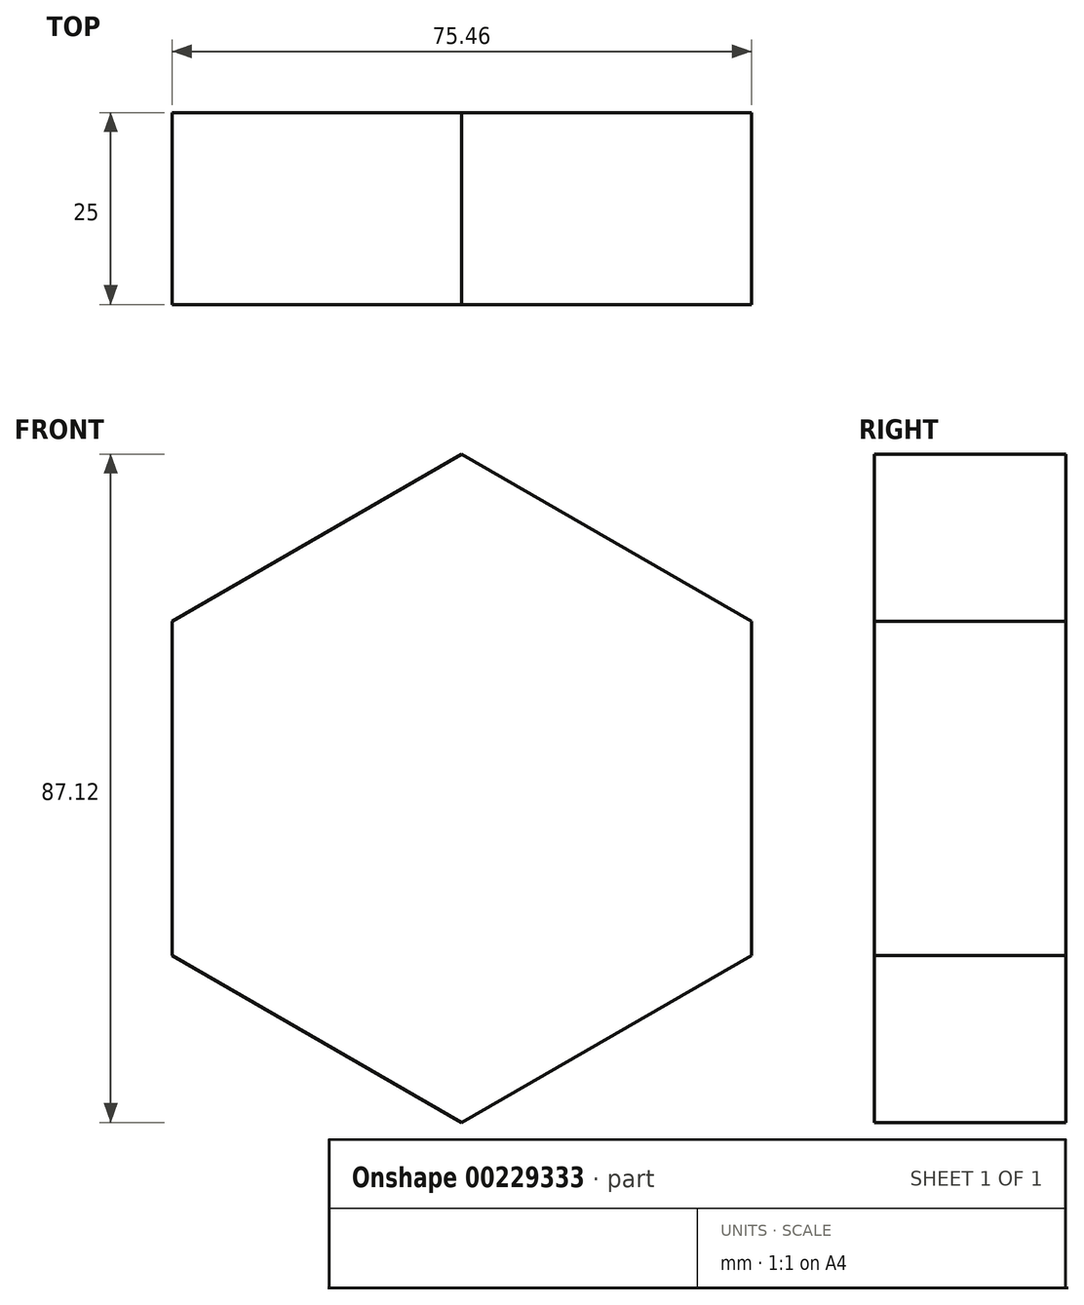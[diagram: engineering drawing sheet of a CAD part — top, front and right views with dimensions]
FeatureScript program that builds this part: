
annotation { "Feature Type Name" : "Feature", "Feature Type Description" : "" }
export const myFeature = defineFeature(function(context is Context, id is Id, definition is map)
    precondition{}
    {
        {
            var Q0;
            Q0=qCreatedBy(makeId("Front.planeOp"),FACE);
            var sketch = newSketch(context, id + "F0", { "sketchPlane" : qUnion([Q0])});
            skCircle(sketch, "E0.cCircle", {"center": v(0, 0) * mm, "radius": 37.73 * mm, "construction": true});
            skLineSegment(sketch, "E0.0", {"start": v(-37.73, -21.78) * mm, "end": v(-37.73, 21.78) * mm});
            skLineSegment(sketch, "E0.1", {"start": v(-37.73, 21.78) * mm, "end": v(0, 43.56) * mm});
            skLineSegment(sketch, "E0.2", {"start": v(0, 43.56) * mm, "end": v(37.73, 21.78) * mm});
            skLineSegment(sketch, "E0.3", {"start": v(37.73, 21.78) * mm, "end": v(37.73, -21.78) * mm});
            skLineSegment(sketch, "E0.4", {"start": v(37.73, -21.78) * mm, "end": v(0, -43.56) * mm});
            skLineSegment(sketch, "E0.5", {"start": v(0, -43.56) * mm, "end": v(-37.73, -21.78) * mm});
            skPoint(sketch, "E0.0.midPoint", {"position": v(-37.73, 0) * mm});
            skSolve(sketch);
        }
        {
            var Q0;
            Q0=makeQuery(id+"F0.imprint","IMPRINT",FACE,{"disambiguationData":[TD([[makeQuery(id+"F0.imprint","IMPRINT",EDGE,{"derivedFrom":sQuery(id+"F0.wireOp",EDGE,"E0.0")}),-1.0]])]});
            extrude(context, id + "F1", {"entities" : qUnion([Q0]), "depth" : 25 * mm});
        }
    });
